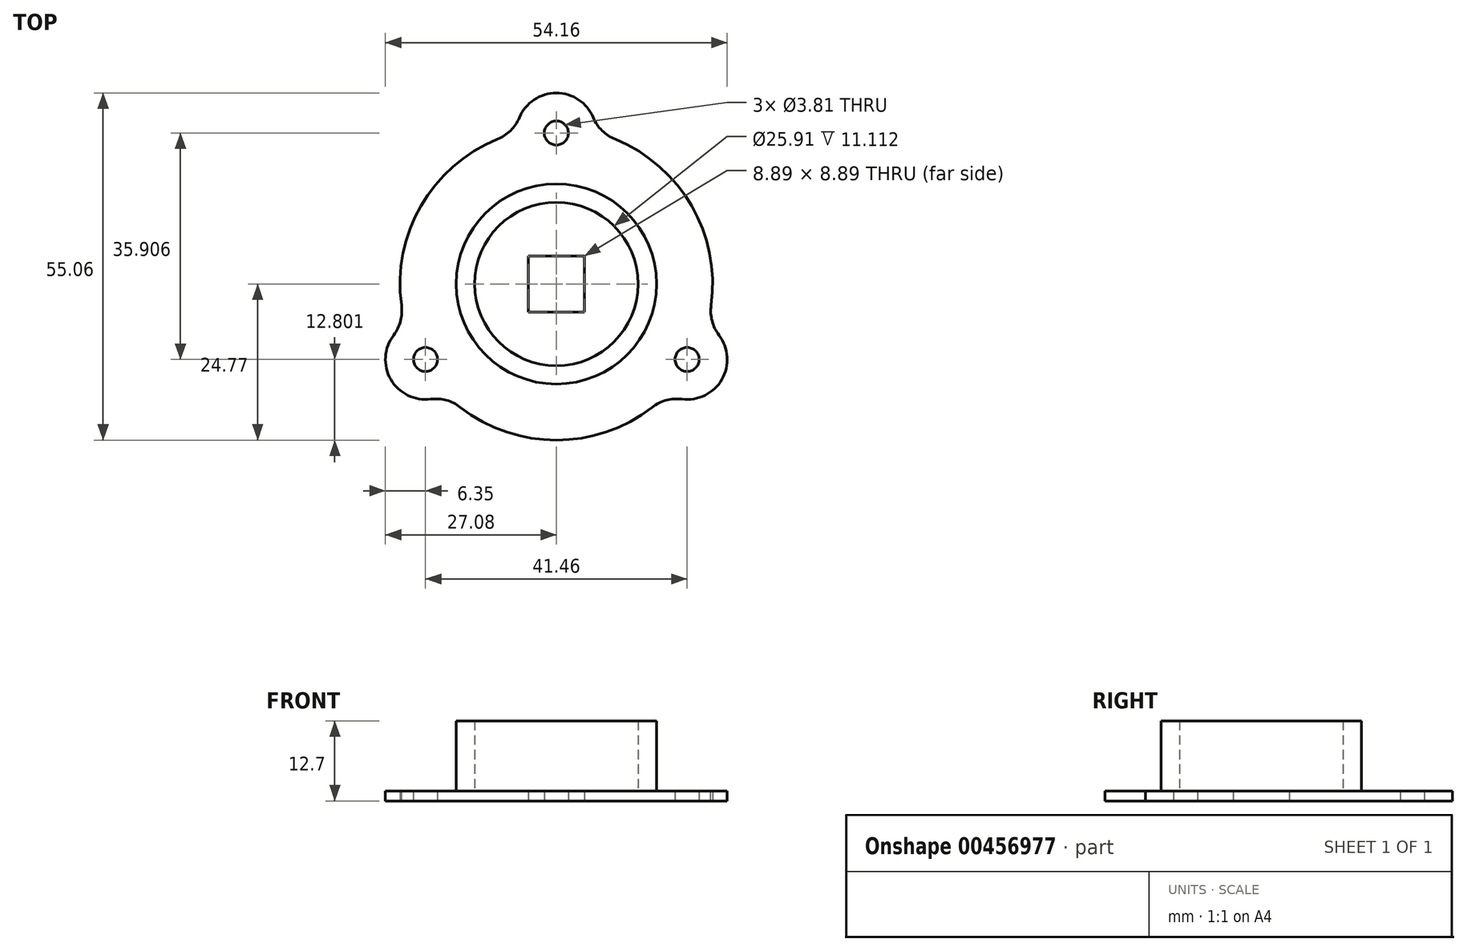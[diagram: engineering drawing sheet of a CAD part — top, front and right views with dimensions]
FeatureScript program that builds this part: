
annotation { "Feature Type Name" : "Feature", "Feature Type Description" : "" }
export const myFeature = defineFeature(function(context is Context, id is Id, definition is map)
    precondition{}
    {
        {
            var Q0;
            Q0=qCreatedBy(makeId("Top.planeOp"),FACE);
            var sketch = newSketch(context, id + "F0", { "sketchPlane" : qUnion([Q0])});
            skCircle(sketch, "E0", {"center": v(0, 0) * mm, "radius": 15.88 * mm});
            skCircle(sketch, "E1", {"center": v(0, 0) * mm, "radius": 24.77 * mm});
            skLineSegment(sketch, "E2", {"start": v(0, 0) * mm, "end": v(0, 42.77) * mm, "construction": true});
            skLineSegment(sketch, "E3", {"start": v(0, 0) * mm, "end": v(-43.71, -25.24) * mm, "construction": true});
            skLineSegment(sketch, "E4", {"start": v(0, 0) * mm, "end": v(46.9, -27.08) * mm, "construction": true});
            skLineSegment(sketch, "E5", {"start": v(-6.35, 2.16) * mm, "end": v(-6.35, 48.97) * mm, "construction": true});
            skLineSegment(sketch, "E6.MirrorCS", {"start": v(6.35, 2.16) * mm, "end": v(6.35, 48.97) * mm, "construction": true});
            skLineSegment(sketch, "E7", {"start": v(-11.23, 0.85) * mm, "end": v(-48.99, -20.95) * mm, "construction": true});
            skLineSegment(sketch, "E8.MirrorCS", {"start": v(-4.88, -10.15) * mm, "end": v(-42.64, -31.95) * mm, "construction": true});
            skLineSegment(sketch, "E9", {"start": v(0.14, -7.41) * mm, "end": v(38.48, -29.55) * mm, "construction": true});
            skLineSegment(sketch, "E10.MirrorCS", {"start": v(6.49, 3.59) * mm, "end": v(44.83, -18.55) * mm, "construction": true});
            skArc(sketch, "E11", {"start": v(6.35, 23.94) * mm, "mid": v(0, 30.29) * mm, "end": v(-6.35, 23.94) * mm});
            skArc(sketch, "E12", {"start": v(-23.9, -6.47) * mm, "mid": v(-26.23, -15.14) * mm, "end": v(-17.56, -17.47) * mm});
            skArc(sketch, "E13", {"start": v(17.56, -17.47) * mm, "mid": v(26.23, -15.14) * mm, "end": v(23.9, -6.47) * mm});
            skCircle(sketch, "E14", {"center": v(0, 23.94) * mm, "radius": 1.9 * mm});
            skCircle(sketch, "E15", {"center": v(-20.73, -11.97) * mm, "radius": 1.9 * mm});
            skCircle(sketch, "E16", {"center": v(20.73, -11.97) * mm, "radius": 1.9 * mm});
            skCircle(sketch, "E17", {"center": v(0, 0) * mm, "radius": 12.95 * mm});
            skLineSegment(sketch, "E18.bottom", {"start": v(-4.45, 4.45) * mm, "end": v(4.44, 4.45) * mm});
            skLineSegment(sketch, "E18.top", {"start": v(-4.45, -4.45) * mm, "end": v(4.45, -4.45) * mm});
            skLineSegment(sketch, "E18.left", {"start": v(-4.45, 4.45) * mm, "end": v(-4.45, -4.45) * mm});
            skLineSegment(sketch, "E18.right", {"start": v(4.45, 4.45) * mm, "end": v(4.45, -4.45) * mm});
            skSolve(sketch);
        }
        {
            var Q0;
            Q0=makeQuery(id+"F0.imprint","IMPRINT",FACE,{"disambiguationData":[TD([[makeQuery(id+"F0.imprint","IMPRINT",EDGE,{"derivedFrom":sQuery(id+"F0.wireOp",EDGE,"E0")}),1.0]])]});
            extrude(context, id + "F1", {"entities" : qUnion([Q0]), "depth" : 12.7 * mm});
        }
        {
            var Q0;
            Q0=makeQuery(id+"F0.imprint","IMPRINT",FACE,{"disambiguationData":[TD([[makeQuery(id+"F0.imprint","IMPRINT",EDGE,{"derivedFrom":sQuery(id+"F0.wireOp",EDGE,"E17")}),1.0]])]});
            extrude(context, id + "F2", {"entities" : qUnion([Q0]), "operationType" : NewBodyOperationType.ADD, "depth" : 1.59 * mm});
        }
        {
            var Q0;
            Q0=makeQuery(id+"F0.imprint","IMPRINT",FACE,{"disambiguationData":[TD([[makeQuery(id+"F0.imprint","IMPRINT",EDGE,{"derivedFrom":sQuery(id+"F0.wireOp",EDGE,"E0")}),-1.0]])]});
            var Q1;
            {var subQ0=sQuery(id+"F0.wireOp",EDGE,"E11");Q1=makeQuery(id+"F0.imprint","IMPRINT",FACE,{"disambiguationData":[TD([[makeQuery(id+"F0.imprint","IMPRINT",EDGE,{"derivedFrom":subQ0}),1.0]])]});}
            var Q2;
            {var subQ0=sQuery(id+"F0.wireOp",EDGE,"E13");Q2=makeQuery(id+"F0.imprint","IMPRINT",FACE,{"disambiguationData":[TD([[makeQuery(id+"F0.imprint","IMPRINT",EDGE,{"derivedFrom":subQ0}),1.0]])]});}
            var Q3;
            {var subQ0=sQuery(id+"F0.wireOp",EDGE,"E12");Q3=makeQuery(id+"F0.imprint","IMPRINT",FACE,{"disambiguationData":[TD([[makeQuery(id+"F0.imprint","IMPRINT",EDGE,{"derivedFrom":subQ0}),1.0]])]});}
            extrude(context, id + "F3", {"entities" : qUnion([Q0, Q1, Q2, Q3]), "operationType" : NewBodyOperationType.ADD, "depth" : 1.59 * mm});
        }
        {
            var Q0;
            {var subQ0=sQuery(id+"F0.wireOp",EDGE,"E12");var subQ1=sQuery(id+"F0.wireOp",EDGE,"E1");Q0=makeQuery(id+"F3.opExtrude","SWEPT_EDGE",EDGE,{"disambiguationData":[OSD([subQ1,subQ0]),TDD([makeQuery(id+"F0.imprint","INTERSECT",VERTEX,{"disambiguationData":[OD(0.0)],"derivedFrom":[subQ1,subQ0]})])]});}
            var Q1;
            {var subQ0=sQuery(id+"F0.wireOp",EDGE,"E12");var subQ1=sQuery(id+"F0.wireOp",EDGE,"E1");Q1=makeQuery(id+"F3.opExtrude","SWEPT_EDGE",EDGE,{"disambiguationData":[OSD([subQ1,subQ0]),TDD([makeQuery(id+"F0.imprint","INTERSECT",VERTEX,{"disambiguationData":[OD(1.0)],"derivedFrom":[subQ1,subQ0]})])]});}
            var Q2;
            {var subQ0=sQuery(id+"F0.wireOp",EDGE,"E13");var subQ1=sQuery(id+"F0.wireOp",EDGE,"E1");Q2=makeQuery(id+"F3.opExtrude","SWEPT_EDGE",EDGE,{"disambiguationData":[OSD([subQ1,subQ0]),TDD([makeQuery(id+"F0.imprint","INTERSECT",VERTEX,{"disambiguationData":[OD(0.0)],"derivedFrom":[subQ1,subQ0]})])]});}
            var Q3;
            {var subQ0=sQuery(id+"F0.wireOp",EDGE,"E13");var subQ1=sQuery(id+"F0.wireOp",EDGE,"E1");Q3=makeQuery(id+"F3.opExtrude","SWEPT_EDGE",EDGE,{"disambiguationData":[OSD([subQ1,subQ0]),TDD([makeQuery(id+"F0.imprint","INTERSECT",VERTEX,{"disambiguationData":[OD(1.0)],"derivedFrom":[subQ1,subQ0]})])]});}
            var Q4;
            {var subQ0=sQuery(id+"F0.wireOp",EDGE,"E11");var subQ1=sQuery(id+"F0.wireOp",EDGE,"E1");Q4=makeQuery(id+"F3.opExtrude","SWEPT_EDGE",EDGE,{"disambiguationData":[OSD([subQ1,subQ0]),TDD([makeQuery(id+"F0.imprint","INTERSECT",VERTEX,{"disambiguationData":[OD(0.0)],"derivedFrom":[subQ1,subQ0]})])]});}
            var Q5;
            {var subQ0=sQuery(id+"F0.wireOp",EDGE,"E11");var subQ1=sQuery(id+"F0.wireOp",EDGE,"E1");Q5=makeQuery(id+"F3.opExtrude","SWEPT_EDGE",EDGE,{"disambiguationData":[OSD([subQ1,subQ0]),TDD([makeQuery(id+"F0.imprint","INTERSECT",VERTEX,{"disambiguationData":[OD(1.0)],"derivedFrom":[subQ1,subQ0]})])]});}
            fillet(context, id + "F4", {"entities" : qUnion([Q0, Q1, Q2, Q3, Q4, Q5]), "radius" : 6.35 * mm, "tangentPropagation" : true, "allowEdgeOverflow" : false});
        }
    });
